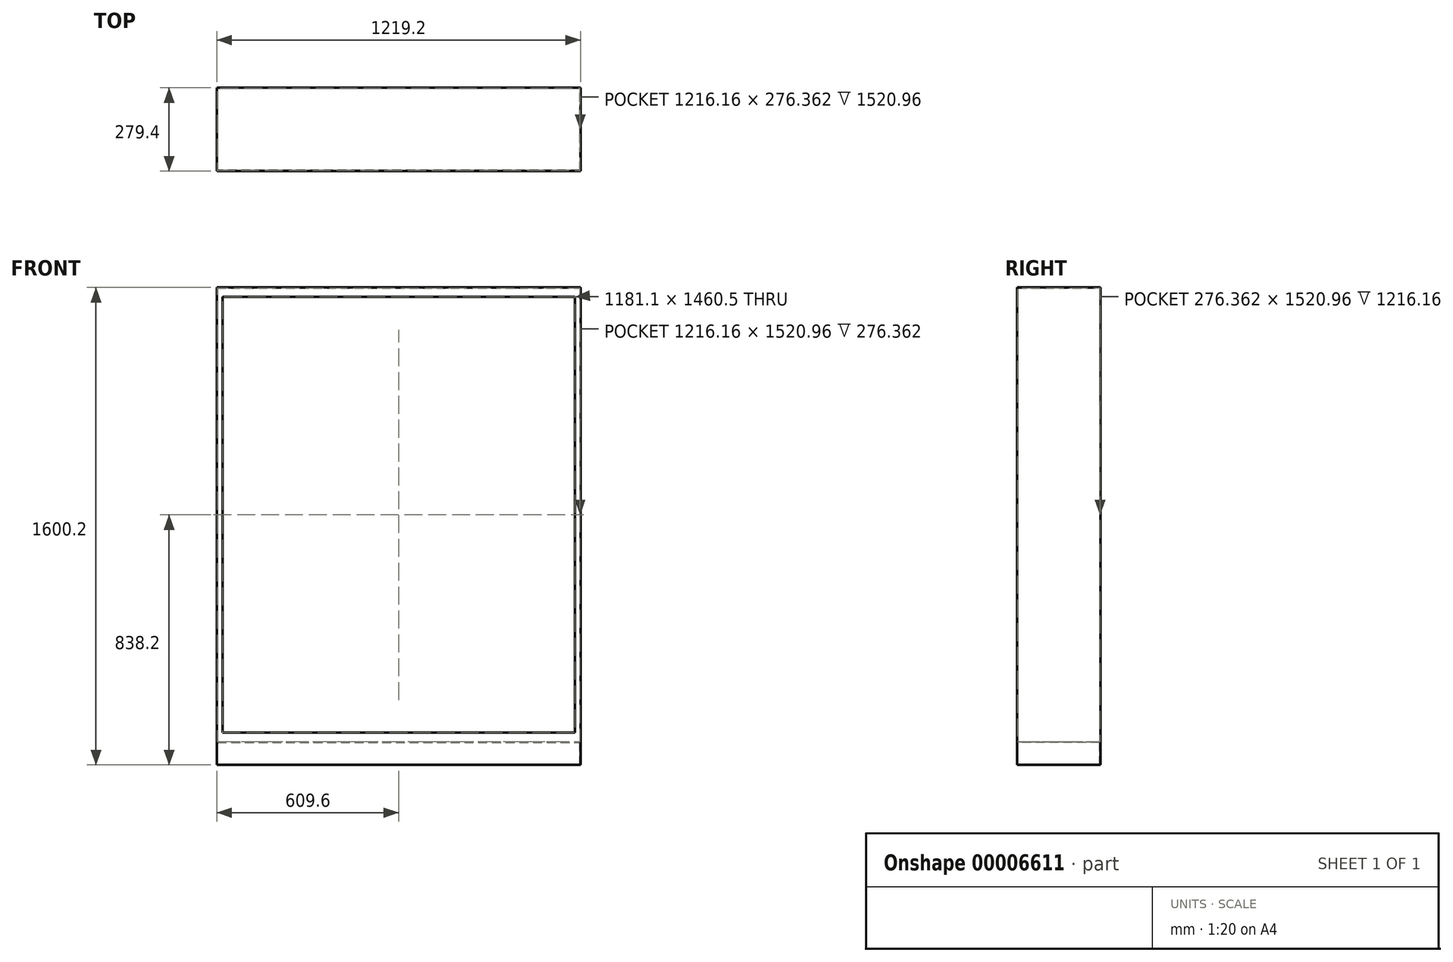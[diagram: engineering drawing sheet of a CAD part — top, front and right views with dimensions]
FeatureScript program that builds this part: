
annotation { "Feature Type Name" : "Feature", "Feature Type Description" : "" }
export const myFeature = defineFeature(function(context is Context, id is Id, definition is map)
    precondition{}
    {
        {
            var Q0;
            Q0=qCreatedBy(makeId("Front.planeOp"),FACE);
            var sketch = newSketch(context, id + "F0", { "sketchPlane" : qUnion([Q0])});
            skLineSegment(sketch, "E0.bottom", {"start": v(0, 0) * mm, "end": v(-1219.2, 0) * mm});
            skLineSegment(sketch, "E0.top", {"start": v(0, 1524) * mm, "end": v(-1219.2, 1524) * mm});
            skLineSegment(sketch, "E0.left", {"start": v(0, 0) * mm, "end": v(0, 1524) * mm});
            skLineSegment(sketch, "E0.right", {"start": v(-1219.2, 0) * mm, "end": v(-1219.2, 1524) * mm});
            skSolve(sketch);
        }
        {
            var Q0;
            Q0 = qSketchRegion(id + "F0", true);
            extrude(context, id + "F1", {"entities" : qUnion([Q0]), "depth" : 279.4 * mm});
        }
        {
            var Q0;
            Q0=makeQuery(id+"F1.opExtrude","CAP_FACE",FACE,{"disambiguationData":[OSD([sQuery(id+"F0.wireOp",EDGE,"E0.bottom"),sQuery(id+"F0.wireOp",EDGE,"E0.top"),sQuery(id+"F0.wireOp",EDGE,"E0.left"),sQuery(id+"F0.wireOp",EDGE,"E0.right")])],"isStart":false});
            shell(context, id + "F2", {"entities" : qUnion([Q0]), "thickness" : 1.52 * mm});
        }
        {
            var Q0;
            Q0=makeQuery(id+"F1.opExtrude","CAP_FACE",FACE,{"disambiguationData":[OSD([sQuery(id+"F0.wireOp",EDGE,"E0.bottom"),sQuery(id+"F0.wireOp",EDGE,"E0.top"),sQuery(id+"F0.wireOp",EDGE,"E0.left"),sQuery(id+"F0.wireOp",EDGE,"E0.right")])],"isStart":true});
            cPlane(context, id + "F3", {"entities" : qUnion([Q0]), "cplaneType" : CPlaneType.OFFSET, "offset" : 279.4 * mm, "oppositeDirection" : true, "width" : 152.4 * mm, "height" : 152.4 * mm});
        }
        {
            var Q0;
            Q0=qCreatedBy(id+"F3.planeOp",FACE);
            var sketch = newSketch(context, id + "F4", { "sketchPlane" : qUnion([Q0])});
            skLineSegment(sketch, "E1.bottom", {"start": v(0, 1524) * mm, "end": v(1219.2, 1524) * mm});
            skLineSegment(sketch, "E1.top", {"start": v(0, 0) * mm, "end": v(1219.2, 0) * mm});
            skLineSegment(sketch, "E1.left", {"start": v(0, 1524) * mm, "end": v(0, 0) * mm});
            skLineSegment(sketch, "E1.right", {"start": v(1219.2, 1524) * mm, "end": v(1219.2, 0) * mm});
            skLineSegment(sketch, "E2.bottom", {"start": v(19.05, 1492.25) * mm, "end": v(1200.15, 1492.25) * mm});
            skLineSegment(sketch, "E2.top", {"start": v(19.05, 31.75) * mm, "end": v(1200.15, 31.75) * mm});
            skLineSegment(sketch, "E2.left", {"start": v(19.05, 1492.25) * mm, "end": v(19.05, 31.75) * mm});
            skLineSegment(sketch, "E2.right", {"start": v(1200.15, 1492.25) * mm, "end": v(1200.15, 31.75) * mm});
            skSolve(sketch);
        }
        {
            var Q0;
            Q0=makeQuery(id+"F4.imprint","IMPRINT",FACE,{"disambiguationData":[TD([[makeQuery(id+"F4.imprint","IMPRINT",EDGE,{"derivedFrom":sQuery(id+"F4.wireOp",EDGE,"E1.bottom")}),-1.0]])]});
            extrude(context, id + "F5", {"entities" : qUnion([Q0]), "operationType" : NewBodyOperationType.ADD, "depth" : 1.52 * mm});
        }
        {
            var Q0;
            Q0=makeQuery(id+"F1.opExtrude","SWEPT_FACE",FACE,{"disambiguationData":[OSD([sQuery(id+"F0.wireOp",EDGE,"E0.bottom")])]});
            extrude(context, id + "F6", {"entities" : qUnion([Q0]), "operationType" : NewBodyOperationType.ADD, "depth" : 76.2 * mm});
        }
        {
            var Q0;
            Q0=makeQuery(id+"F6.opExtrude","CAP_FACE",FACE,{"disambiguationData":[OSD([sQuery(id+"F0.wireOp",EDGE,"E0.bottom")])],"isStart":false});
            shell(context, id + "F7", {"entities" : qUnion([Q0]), "thickness" : 2.54 * mm});
        }
    });
